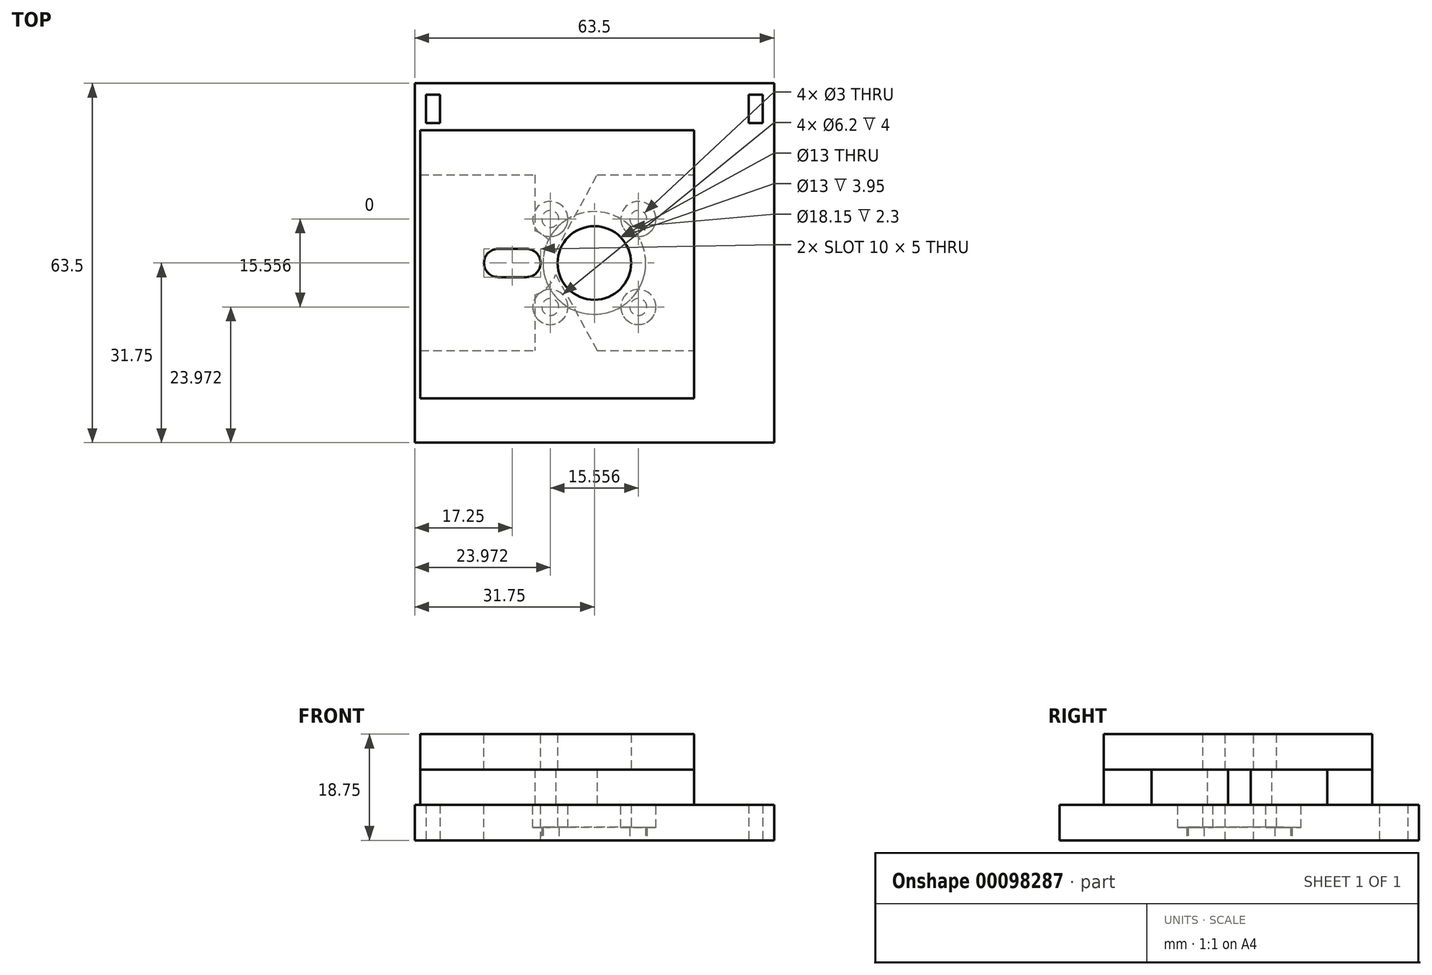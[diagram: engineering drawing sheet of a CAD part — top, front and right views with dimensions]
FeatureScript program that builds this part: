
annotation { "Feature Type Name" : "Feature", "Feature Type Description" : "" }
export const myFeature = defineFeature(function(context is Context, id is Id, definition is map)
    precondition{}
    {
        {
            assignVariable(context, id + "F0", {"name" : "baseT", "anyValue" : 6.25});
        }
        {
            assignVariable(context, id + "F1", {"name" : "m3BoltHeadRecess", "anyValue" : 4});
        }
        {
            assignVariable(context, id + "F2", {"name" : "stepperInsetH", "anyValue" : 2.3});
        }
        {
            var Q0;
            Q0=qCreatedBy(makeId("Top.planeOp"),FACE);
            var sketch = newSketch(context, id + "F3", { "sketchPlane" : qUnion([Q0])});
            skCircle(sketch, "E0", {"center": v(0, 0) * mm, "radius": 15 * mm, "construction": true});
            skLineSegment(sketch, "E1.bottom", {"start": v(-29.75, 29.75) * mm, "end": v(-27.25, 29.75) * mm});
            skLineSegment(sketch, "E1.top", {"start": v(-29.75, 24.75) * mm, "end": v(-27.25, 24.75) * mm});
            skLineSegment(sketch, "E1.left", {"start": v(-29.75, 29.75) * mm, "end": v(-29.75, 24.75) * mm});
            skLineSegment(sketch, "E1.right", {"start": v(-27.25, 29.75) * mm, "end": v(-27.25, 24.75) * mm});
            skLineSegment(sketch, "E2.bottom", {"start": v(29.75, 29.75) * mm, "end": v(27.25, 29.75) * mm});
            skLineSegment(sketch, "E2.top", {"start": v(29.75, 24.75) * mm, "end": v(27.25, 24.75) * mm});
            skLineSegment(sketch, "E2.left", {"start": v(29.75, 29.75) * mm, "end": v(29.75, 24.75) * mm});
            skLineSegment(sketch, "E2.right", {"start": v(27.25, 29.75) * mm, "end": v(27.25, 24.75) * mm});
            skLineSegment(sketch, "E3.1", {"start": v(-31.75, 31.75) * mm, "end": v(-31.75, -31.75) * mm});
            skLineSegment(sketch, "E3.2", {"start": v(-31.75, 31.75) * mm, "end": v(-27.25, 31.75) * mm});
            skLineSegment(sketch, "E4.0", {"start": v(31.75, 31.75) * mm, "end": v(27.25, 31.75) * mm});
            skLineSegment(sketch, "E4.1", {"start": v(31.75, 31.75) * mm, "end": v(31.75, -31.75) * mm});
            skLineSegment(sketch, "E5.right", {"start": v(-1, 28.46) * mm, "end": v(-1, -26.52) * mm, "construction": true});
            skLineSegment(sketch, "E6", {"start": v(-27.25, 31.75) * mm, "end": v(27.25, 31.75) * mm});
            skCircle(sketch, "E7", {"center": v(0, 0) * mm, "radius": 11 * mm, "construction": true});
            skCircle(sketch, "E8", {"center": v(-7.78, 7.78) * mm, "radius": 1.5 * mm});
            skCircle(sketch, "E9.1.0", {"center": v(-7.78, -7.78) * mm, "radius": 1.5 * mm});
            skCircle(sketch, "E9.2.0", {"center": v(7.78, -7.78) * mm, "radius": 1.5 * mm});
            skCircle(sketch, "E9.3.0", {"center": v(7.78, 7.78) * mm, "radius": 1.5 * mm});
            skCircle(sketch, "E10", {"center": v(-7.78, 7.78) * mm, "radius": 4.6 * mm, "construction": true});
            skCircle(sketch, "E11.1.0", {"center": v(-7.78, -7.78) * mm, "radius": 4.6 * mm, "construction": true});
            skCircle(sketch, "E11.2.0", {"center": v(7.78, -7.78) * mm, "radius": 4.6 * mm, "construction": true});
            skCircle(sketch, "E11.3.0", {"center": v(7.78, 7.78) * mm, "radius": 4.6 * mm, "construction": true});
            skLineSegment(sketch, "E12", {"start": v(31.75, -31.75) * mm, "end": v(-31.75, -31.75) * mm});
            skPoint(sketch, "E13.endSnap0", {"position": v(-27.25, 27.25) * mm});
            skCircle(sketch, "E14", {"center": v(0, 0) * mm, "radius": 6.5 * mm});
            skSolve(sketch);
        }
        {
            var Q0;
            Q0=makeQuery(id+"F3.imprint","IMPRINT",FACE,{"disambiguationData":[TD([[makeQuery(id+"F3.imprint","IMPRINT",EDGE,{"derivedFrom":sQuery(id+"F3.wireOp",EDGE,"E1.bottom")}),1.0]])]});
            extrude(context, id + "F4", {"entities" : qUnion([Q0]), "depth" : (getVariable(context, 'baseT')) * mm});
        }
        {
            var Q0;
            Q0=makeQuery(id+"F4.opExtrude","CAP_FACE",FACE,{"disambiguationData":[OSD([sQuery(id+"F3.wireOp",EDGE,"E1.bottom"),sQuery(id+"F3.wireOp",EDGE,"E1.top"),sQuery(id+"F3.wireOp",EDGE,"E1.left"),sQuery(id+"F3.wireOp",EDGE,"E1.right"),sQuery(id+"F3.wireOp",EDGE,"E2.bottom"),sQuery(id+"F3.wireOp",EDGE,"E2.top"),sQuery(id+"F3.wireOp",EDGE,"E2.left"),sQuery(id+"F3.wireOp",EDGE,"E2.right"),sQuery(id+"F3.wireOp",EDGE,"E3.0"),sQuery(id+"F3.wireOp",EDGE,"E3.1"),sQuery(id+"F3.wireOp",EDGE,"E3.2"),sQuery(id+"F3.wireOp",EDGE,"E4.0"),sQuery(id+"F3.wireOp",EDGE,"E4.1"),sQuery(id+"F3.wireOp",EDGE,"E4.2"),sQuery(id+"F3.wireOp",EDGE,"E6"),sQuery(id+"F3.wireOp",EDGE,"E8"),sQuery(id+"F3.wireOp",EDGE,"E9.1.0"),sQuery(id+"F3.wireOp",EDGE,"E9.2.0"),sQuery(id+"F3.wireOp",EDGE,"E9.3.0"),sQuery(id+"F3.wireOp",EDGE,"Mi6dx3AY-uMIZ-Df3I-gBde-4dB2NnZOwbx9"),sQuery(id+"F3.wireOp",EDGE,"E12"),sQuery(id+"F3.wireOp",EDGE,"He8D96uv-mS6Q-57cv-aHRz-I5kNUTtSJCBH"),sQuery(id+"F3.wireOp",EDGE,"E13"),sQuery(id+"F3.wireOp",EDGE,"wjEPWtgr-vBOl-Kljx-w1dd-p7NBxDcS8vAf"),sQuery(id+"F3.wireOp",EDGE,"PLWTT3C3-2iGu-kcem-znEJ-QKxlFtEV3tnr"),sQuery(id+"F3.wireOp",EDGE,"2zCN3ppK-VHyn-6Quy-Bxkh-GUdytJ533KvV"),sQuery(id+"F3.wireOp",EDGE,"iCG1O4UW-Ieoe-LlZV-2Yi0-UEBVlfb5CP1r"),sQuery(id+"F3.wireOp",EDGE,"E14")])],"isStart":false});
            var sketch = newSketch(context, id + "F5", { "sketchPlane" : qUnion([Q0])});
            skCircle(sketch, "E15", {"center": v(-7.78, 7.78) * mm, "radius": 3.1 * mm});
            skCircle(sketch, "E16.1.0", {"center": v(-7.78, -7.78) * mm, "radius": 3.1 * mm});
            skCircle(sketch, "E16.2.0", {"center": v(7.78, -7.78) * mm, "radius": 3.1 * mm});
            skCircle(sketch, "E16.3.0", {"center": v(7.78, 7.78) * mm, "radius": 3.1 * mm});
            skPoint(sketch, "E16.center", {"position": v(0, 0) * mm});
            skSolve(sketch);
        }
        {
            var Q0;
            Q0=qSketchRegion(id+"F5",true);
            extrude(context, id + "F6", {"entities" : qUnion([Q0]), "operationType" : NewBodyOperationType.REMOVE, "oppositeDirection" : true, "depth" : (getVariable(context, 'm3BoltHeadRecess')) * mm});
        }
        {
            var Q0;
            Q0=makeQuery(id+"F4.opExtrude","CAP_FACE",FACE,{"disambiguationData":[OSD([sQuery(id+"F3.wireOp",EDGE,"E1.bottom"),sQuery(id+"F3.wireOp",EDGE,"E1.top"),sQuery(id+"F3.wireOp",EDGE,"E1.left"),sQuery(id+"F3.wireOp",EDGE,"E1.right"),sQuery(id+"F3.wireOp",EDGE,"E2.bottom"),sQuery(id+"F3.wireOp",EDGE,"E2.top"),sQuery(id+"F3.wireOp",EDGE,"E2.left"),sQuery(id+"F3.wireOp",EDGE,"E2.right"),sQuery(id+"F3.wireOp",EDGE,"E3.0"),sQuery(id+"F3.wireOp",EDGE,"E3.1"),sQuery(id+"F3.wireOp",EDGE,"E3.2"),sQuery(id+"F3.wireOp",EDGE,"E4.0"),sQuery(id+"F3.wireOp",EDGE,"E4.1"),sQuery(id+"F3.wireOp",EDGE,"E4.2"),sQuery(id+"F3.wireOp",EDGE,"E6"),sQuery(id+"F3.wireOp",EDGE,"E8"),sQuery(id+"F3.wireOp",EDGE,"E9.1.0"),sQuery(id+"F3.wireOp",EDGE,"E9.2.0"),sQuery(id+"F3.wireOp",EDGE,"E9.3.0"),sQuery(id+"F3.wireOp",EDGE,"Mi6dx3AY-uMIZ-Df3I-gBde-4dB2NnZOwbx9"),sQuery(id+"F3.wireOp",EDGE,"E12"),sQuery(id+"F3.wireOp",EDGE,"He8D96uv-mS6Q-57cv-aHRz-I5kNUTtSJCBH"),sQuery(id+"F3.wireOp",EDGE,"E13"),sQuery(id+"F3.wireOp",EDGE,"wjEPWtgr-vBOl-Kljx-w1dd-p7NBxDcS8vAf"),sQuery(id+"F3.wireOp",EDGE,"PLWTT3C3-2iGu-kcem-znEJ-QKxlFtEV3tnr"),sQuery(id+"F3.wireOp",EDGE,"2zCN3ppK-VHyn-6Quy-Bxkh-GUdytJ533KvV"),sQuery(id+"F3.wireOp",EDGE,"iCG1O4UW-Ieoe-LlZV-2Yi0-UEBVlfb5CP1r"),sQuery(id+"F3.wireOp",EDGE,"E14")])],"isStart":true});
            var sketch = newSketch(context, id + "F7", { "sketchPlane" : qUnion([Q0])});
            skCircle(sketch, "E17", {"center": v(0, 0) * mm, "radius": 9.07 * mm});
            skSolve(sketch);
        }
        {
            var Q0;
            Q0=makeQuery(id+"F7.imprint","IMPRINT",FACE,{"disambiguationData":[TD([[makeQuery(id+"F7.imprint","IMPRINT",EDGE,{"derivedFrom":sQuery(id+"F7.wireOp",EDGE,"E17")}),1.0]])]});
            extrude(context, id + "F8", {"entities" : qUnion([Q0]), "operationType" : NewBodyOperationType.REMOVE, "oppositeDirection" : true, "depth" : (getVariable(context, 'stepperInsetH')) * mm});
        }
        {
            var Q0;
            Q0=makeQuery(id+"F4.opExtrude","CAP_FACE",FACE,{"disambiguationData":[OSD([sQuery(id+"F3.wireOp",EDGE,"E1.bottom"),sQuery(id+"F3.wireOp",EDGE,"E1.top"),sQuery(id+"F3.wireOp",EDGE,"E1.left"),sQuery(id+"F3.wireOp",EDGE,"E1.right"),sQuery(id+"F3.wireOp",EDGE,"E2.bottom"),sQuery(id+"F3.wireOp",EDGE,"E2.top"),sQuery(id+"F3.wireOp",EDGE,"E2.left"),sQuery(id+"F3.wireOp",EDGE,"E2.right"),sQuery(id+"F3.wireOp",EDGE,"E3.1"),sQuery(id+"F3.wireOp",EDGE,"E3.2"),sQuery(id+"F3.wireOp",EDGE,"E4.0"),sQuery(id+"F3.wireOp",EDGE,"E4.1"),sQuery(id+"F3.wireOp",EDGE,"E6"),sQuery(id+"F3.wireOp",EDGE,"E8"),sQuery(id+"F3.wireOp",EDGE,"E9.1.0"),sQuery(id+"F3.wireOp",EDGE,"E9.2.0"),sQuery(id+"F3.wireOp",EDGE,"E9.3.0"),sQuery(id+"F3.wireOp",EDGE,"E12"),sQuery(id+"F3.wireOp",EDGE,"E14")])],"isStart":false});
            var sketch = newSketch(context, id + "F9", { "sketchPlane" : qUnion([Q0])});
            skLineSegment(sketch, "E18.bottom", {"start": v(-30.75, -15.5) * mm, "end": v(17.62, -15.5) * mm});
            skLineSegment(sketch, "E18.top", {"start": v(-30.75, -23.95) * mm, "end": v(17.62, -23.95) * mm});
            skLineSegment(sketch, "E18.left", {"start": v(-30.75, -15.5) * mm, "end": v(-30.75, -23.95) * mm});
            skLineSegment(sketch, "E18.right", {"start": v(17.62, -15.5) * mm, "end": v(17.62, -23.95) * mm});
            skLineSegment(sketch, "E19.bottom", {"start": v(-30.75, 23.45) * mm, "end": v(17.62, 23.45) * mm});
            skLineSegment(sketch, "E19.top", {"start": v(-30.75, 15.55) * mm, "end": v(17.62, 15.55) * mm});
            skLineSegment(sketch, "E19.left", {"start": v(-30.75, 23.45) * mm, "end": v(-30.75, 15.55) * mm});
            skLineSegment(sketch, "E19.right", {"start": v(17.62, 23.45) * mm, "end": v(17.62, 15.55) * mm});
            skLineSegment(sketch, "E20", {"start": v(-10.5, 15.55) * mm, "end": v(-10.5, 5.66) * mm});
            skLineSegment(sketch, "E21", {"start": v(-10.5, -5.66) * mm, "end": v(-10.5, -15.5) * mm});
            skArc(sketch, "E22", {"start": v(-10.5, -5.66) * mm, "mid": v(-6.5, 0) * mm, "end": v(-10.5, 5.66) * mm});
            skLineSegment(sketch, "E23", {"start": v(-6.84, 2) * mm, "end": v(0.5, 15.55) * mm});
            skLineSegment(sketch, "E24", {"start": v(-6.84, -2) * mm, "end": v(0.5, -15.5) * mm});
            skSolve(sketch);
        }
        {
            var Q0;
            Q0 = qSketchRegion(id + "F9", true);
            extrude(context, id + "F10", {"entities" : qUnion([Q0]), "depth" : (getVariable(context, 'baseT')) * mm});
        }
        {
            var Q0;
            Q0=makeQuery(id+"F10.opExtrude","CAP_FACE",FACE,{"disambiguationData":[OSD([sQuery(id+"F9.wireOp",EDGE,"E19.bottom"),sQuery(id+"F9.wireOp",EDGE,"E19.top"),sQuery(id+"F9.wireOp",EDGE,"E19.left"),sQuery(id+"F9.wireOp",EDGE,"E19.right")])],"isStart":false});
            var sketch = newSketch(context, id + "F11", { "sketchPlane" : qUnion([Q0])});
            skLineSegment(sketch, "E25.bottom", {"start": v(-30.75, 23.45) * mm, "end": v(17.62, 23.45) * mm});
            skLineSegment(sketch, "E25.top", {"start": v(-30.75, -23.95) * mm, "end": v(17.62, -23.95) * mm});
            skLineSegment(sketch, "E25.left", {"start": v(-30.75, 23.45) * mm, "end": v(-30.75, -23.95) * mm});
            skLineSegment(sketch, "E25.right", {"start": v(17.62, 23.45) * mm, "end": v(17.62, -23.95) * mm});
            skCircle(sketch, "E26", {"center": v(0, 0) * mm, "radius": 6.5 * mm});
            skSolve(sketch);
        }
        {
            var Q0;
            {var subQ0=sQuery(id+"F11.wireOp",EDGE,"E25.bottom");Q0=makeQuery(id+"F11.imprint","IMPRINT",FACE,{"disambiguationData":[TD([[makeQuery(id+"F11.imprint","IMPRINT",EDGE,{"derivedFrom":subQ0}),-1.0]])]});}
            var Q1;
            {var subQ0=sQuery(id+"F11.wireOp",EDGE,"E25.top");Q1=makeQuery(id+"F11.imprint","IMPRINT",FACE,{"disambiguationData":[TD([[makeQuery(id+"F11.imprint","IMPRINT",EDGE,{"derivedFrom":subQ0}),1.0]])]});}
            extrude(context, id + "F12", {"entities" : qUnion([Q0, Q1]), "depth" : (getVariable(context, 'baseT')) * mm});
        }
        {
            var Q0;
            Q0=makeQuery(id+"F12.opExtrude","CAP_FACE",FACE,{"disambiguationData":[OSD([sQuery(id+"F11.wireOp",EDGE,"E25.bottom"),sQuery(id+"F11.wireOp",EDGE,"E25.top"),sQuery(id+"F11.wireOp",EDGE,"E25.left"),sQuery(id+"F11.wireOp",EDGE,"E25.right"),sQuery(id+"F11.wireOp",EDGE,"E26")])],"isStart":false});
            var sketch = newSketch(context, id + "F13", { "sketchPlane" : qUnion([Q0])});
            skLineSegment(sketch, "E27", {"start": v(-17, 2.5) * mm, "end": v(-12, 2.5) * mm});
            skLineSegment(sketch, "E28", {"start": v(-17, -2.5) * mm, "end": v(-12, -2.5) * mm});
            skArc(sketch, "E29", {"start": v(-17, 2.5) * mm, "mid": v(-19.5, 0) * mm, "end": v(-17, -2.5) * mm});
            skArc(sketch, "E30", {"start": v(-12, -2.5) * mm, "mid": v(-9.5, 0) * mm, "end": v(-12, 2.5) * mm});
            skSolve(sketch);
        }
        {
            var Q0;
            Q0 = qSketchRegion(id + "F13", true);
            extrude(context, id + "F14", {"entities" : qUnion([Q0]), "operationType" : NewBodyOperationType.REMOVE, "oppositeDirection" : true, "depth" : 25 * mm});
        }
    });
